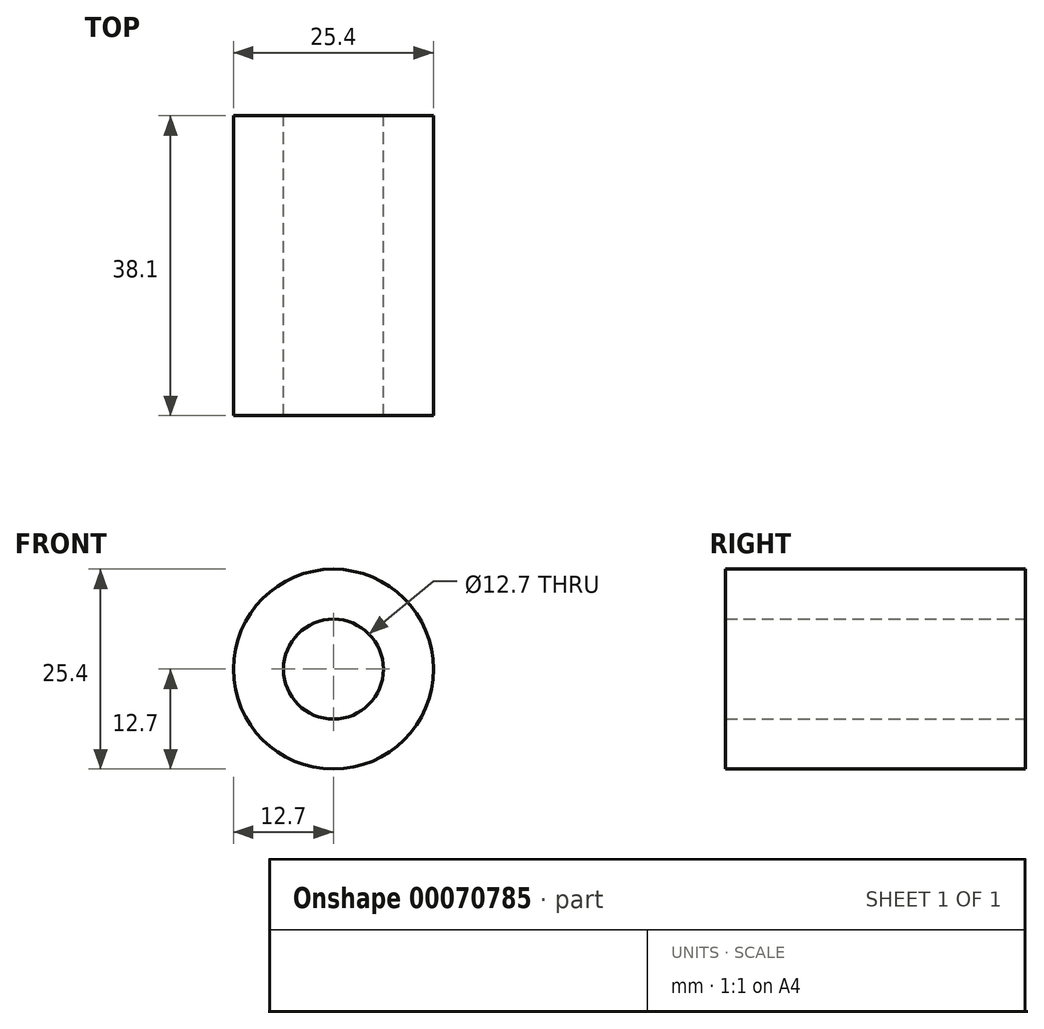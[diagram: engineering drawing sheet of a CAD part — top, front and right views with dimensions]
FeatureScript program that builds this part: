
annotation { "Feature Type Name" : "Feature", "Feature Type Description" : "" }
export const myFeature = defineFeature(function(context is Context, id is Id, definition is map)
    precondition{}
    {
        {
            var Q0;
            Q0=qCreatedBy(makeId("Front.planeOp"),FACE);
            var sketch = newSketch(context, id + "F0", { "sketchPlane" : qUnion([Q0])});
            skCircle(sketch, "E0", {"center": v(0, 0) * mm, "radius": 6.35 * mm});
            skCircle(sketch, "E1", {"center": v(0, 0) * mm, "radius": 12.7 * mm});
            skSolve(sketch);
        }
        {
            var Q0;
            Q0 = qSketchRegion(id + "F0", true);
            extrude(context, id + "F1", {"entities" : qUnion([Q0]), "depth" : 38.1 * mm});
        }
    });
